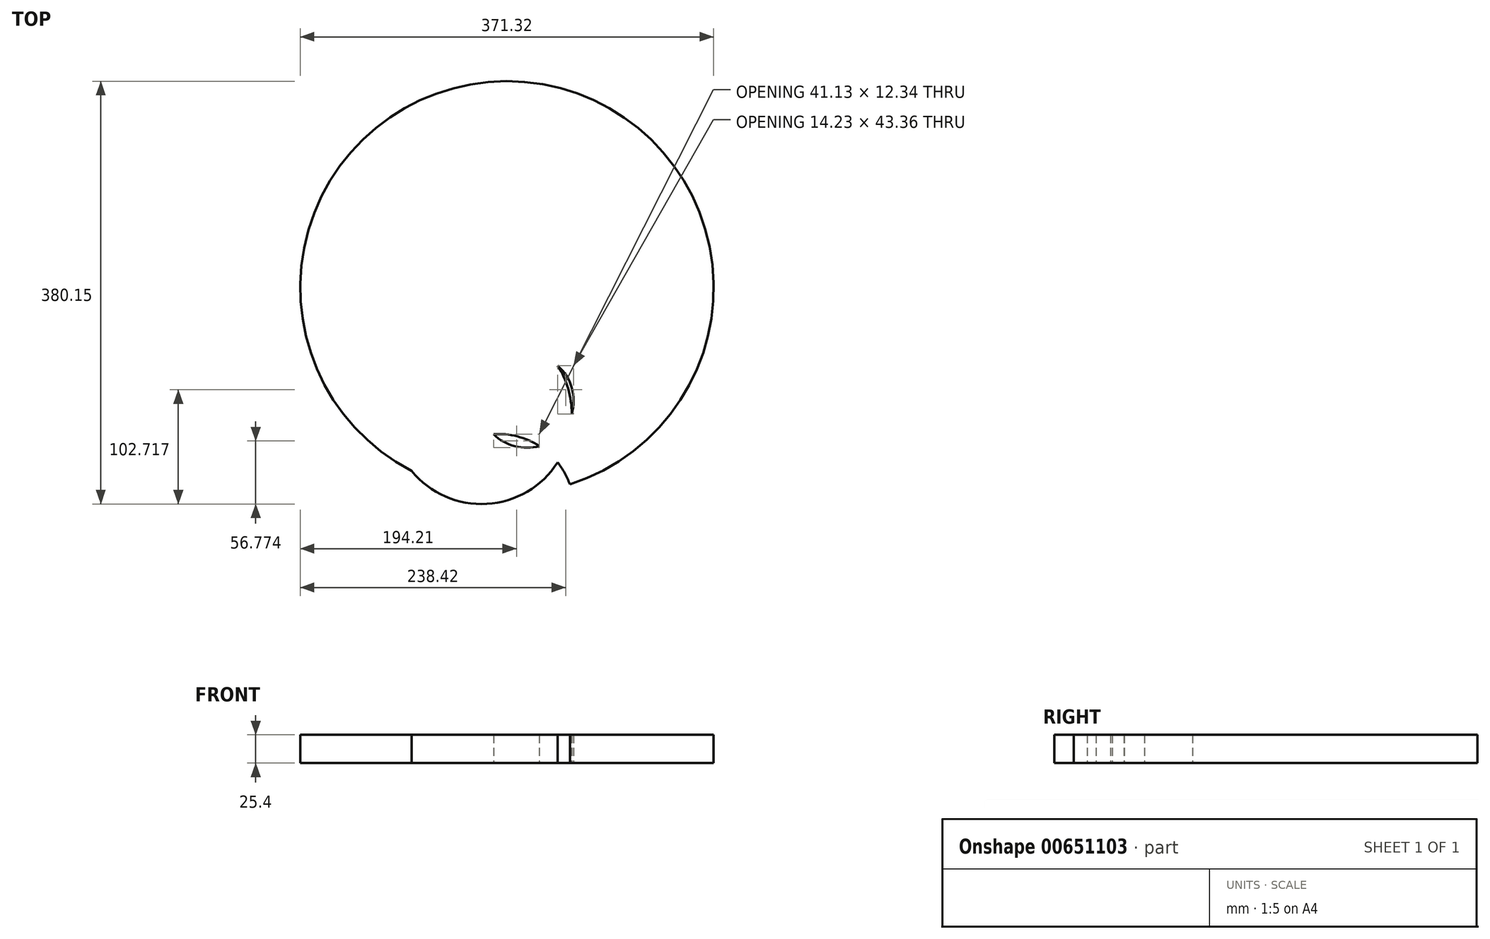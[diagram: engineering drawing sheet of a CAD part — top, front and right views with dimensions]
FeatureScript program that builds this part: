
annotation { "Feature Type Name" : "Feature", "Feature Type Description" : "" }
export const myFeature = defineFeature(function(context is Context, id is Id, definition is map)
    precondition{}
    {
        {
            var Q0;
            Q0=qCreatedBy(makeId("Top.planeOp"),FACE);
            var sketch = newSketch(context, id + "F0", { "sketchPlane" : qUnion([Q0])});
            skLineSegment(sketch, "E0", {"start": v(-46.32, 24.93) * mm, "end": v(-46.32, 35.56) * mm});
            skLineSegment(sketch, "E1", {"start": v(-46.32, 35.56) * mm, "end": v(-20.53, -47.78) * mm});
            skLineSegment(sketch, "E2", {"start": v(-20.53, -47.78) * mm, "end": v(51.08, -44.36) * mm});
            skLineSegment(sketch, "E3", {"start": v(51.08, -44.36) * mm, "end": v(51.08, 39.72) * mm});
            skLineSegment(sketch, "E4", {"start": v(51.08, 39.72) * mm, "end": v(0.49, 65.62) * mm});
            skLineSegment(sketch, "E5", {"start": v(0.49, 65.62) * mm, "end": v(-40.08, 53.65) * mm});
            skLineSegment(sketch, "E6", {"start": v(-40.08, 53.65) * mm, "end": v(-44.97, 40.2) * mm});
            skLineSegment(sketch, "E7", {"start": v(-44.97, 40.2) * mm, "end": v(-47.9, 36.54) * mm});
            skLineSegment(sketch, "E8", {"start": v(-47.9, 36.54) * mm, "end": v(-46.2, 29.2) * mm});
            skSolve(sketch);
        }
        {
            var Q0;
            {var subQ0=sQuery(id+"F0.wireOp",EDGE,"E1");Q0=makeQuery(id+"F0.imprint","IMPRINT",FACE,{"disambiguationData":[TD([[makeQuery(id+"F0.imprint","IMPRINT",EDGE,{"derivedFrom":subQ0}),1.0]])]});}
            var sketch = newSketch(context, id + "F1", { "sketchPlane" : qUnion([Q0])});
            skArc(sketch, "E9", {"start": v(-57.2, 41.67) * mm, "mid": v(80.1, -33.18) * mm, "end": v(0, 101.12) * mm});
            skArc(sketch, "E10", {"start": v(21.7, 23.02) * mm, "mid": v(98.6, 13.36) * mm, "end": v(52.8, 75.89) * mm});
            skArc(sketch, "E11", {"start": v(102.65, -80.53) * mm, "mid": v(48.7, 3.89) * mm, "end": v(-30.8, -57.07) * mm});
            skArc(sketch, "E12", {"start": v(76.5, -46.44) * mm, "mid": v(32.84, 321.74) * mm, "end": v(35.89, -49) * mm});
            skSolve(sketch);
        }
        {
            var Q0;
            Q0 = qSketchRegion(id + "F1", true);
            extrude(context, id + "F2", {"entities" : qUnion([Q0]), "depth" : 25.4 * mm, "offsetDistance" : 25.4 * mm});
        }
    });
